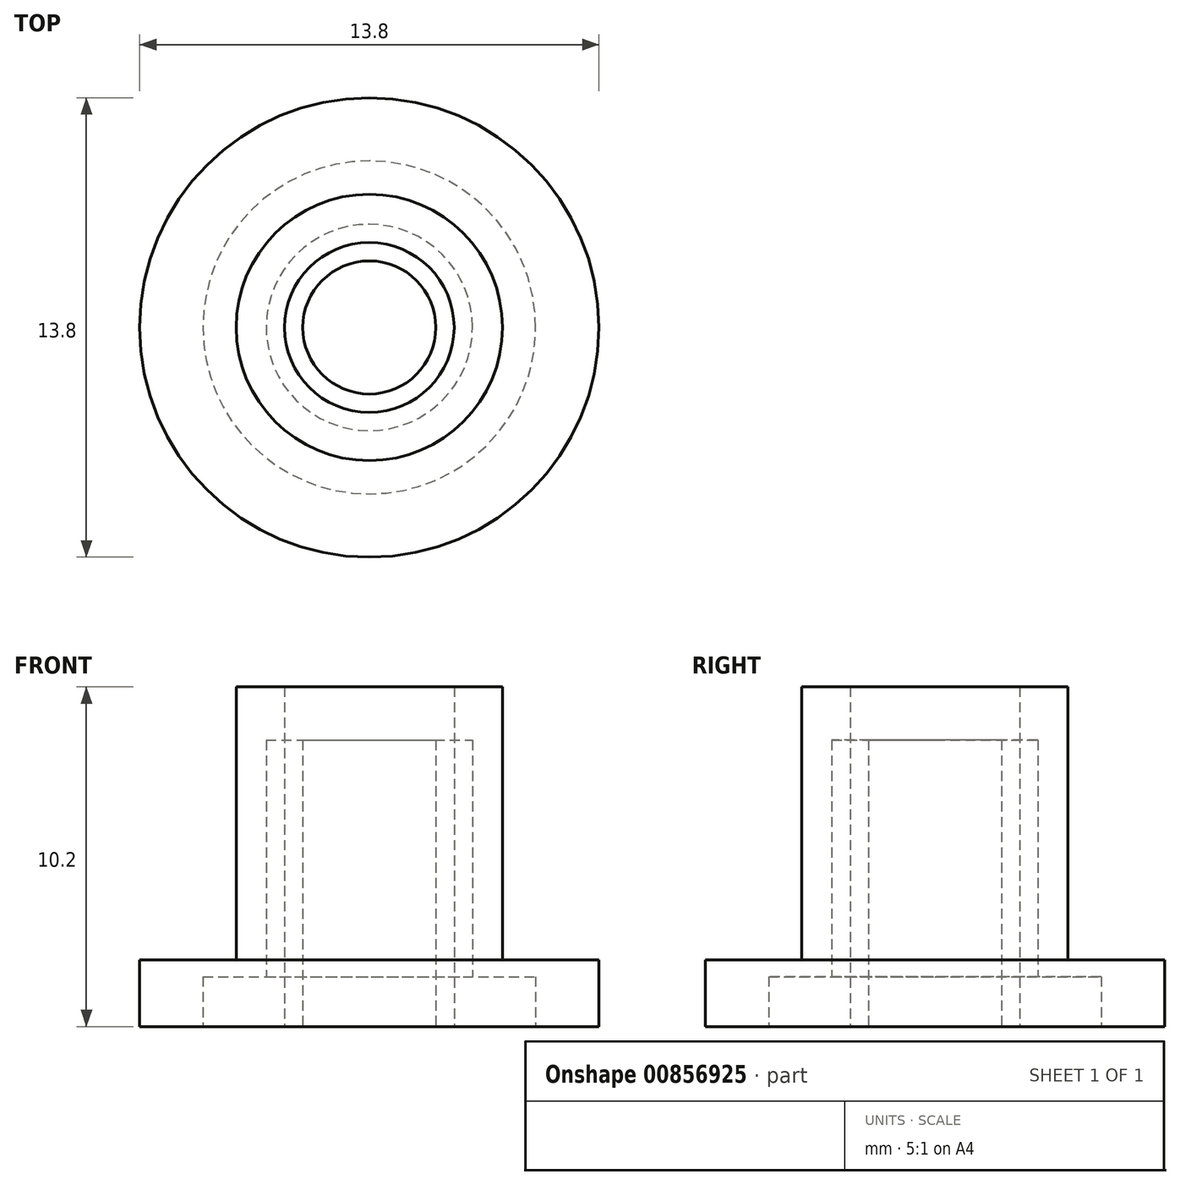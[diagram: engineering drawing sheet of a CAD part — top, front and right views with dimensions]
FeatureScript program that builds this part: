
annotation { "Feature Type Name" : "Feature", "Feature Type Description" : "" }
export const myFeature = defineFeature(function(context is Context, id is Id, definition is map)
    precondition{}
    {
        {
            var Q0;
            Q0=qCreatedBy(makeId("Front.planeOp"),FACE);
            var sketch = newSketch(context, id + "F0", { "sketchPlane" : qUnion([Q0])});
            skLineSegment(sketch, "E0", {"start": v(0, 0) * mm, "end": v(0, 12.5) * mm, "construction": true});
            skLineSegment(sketch, "E1", {"start": v(-2, 0) * mm, "end": v(-2, 8.6) * mm});
            skLineSegment(sketch, "E2", {"start": v(-2, 8.6) * mm, "end": v(-3.1, 8.6) * mm});
            skLineSegment(sketch, "E3", {"start": v(-3.1, 8.6) * mm, "end": v(-3.1, 1.5) * mm});
            skLineSegment(sketch, "E4", {"start": v(-3.1, 1.5) * mm, "end": v(-5, 1.5) * mm});
            skLineSegment(sketch, "E5", {"start": v(-5, 1.5) * mm, "end": v(-5, 0) * mm});
            skLineSegment(sketch, "E6", {"start": v(-5, 0) * mm, "end": v(-2, 0) * mm});
            skSolve(sketch);
        }
        {
            var Q0;
            Q0=makeQuery(id+"F0.imprint","IMPRINT",FACE,{"disambiguationData":[TD([[makeQuery(id+"F0.imprint","IMPRINT",EDGE,{"derivedFrom":sQuery(id+"F0.wireOp",EDGE,"E1")}),1.0]])]});
            var Q1;
            Q1=sQuery(id+"F0.wireOp",EDGE,"E0");
            revolve(context, id + "F1", {"surfaceOperationType" : NewSurfaceOperationType.NEW, "entities" : qUnion([Q0]), "axis" : qUnion([Q1]), "revolveType" : RevolveType.FULL});
        }
        {
            var Q0;
            Q0=qCreatedBy(makeId("Front.planeOp"),FACE);
            var sketch = newSketch(context, id + "F2", { "sketchPlane" : qUnion([Q0])});
            skLineSegment(sketch, "E7", {"start": v(0, 0) * mm, "end": v(0, 9.24) * mm, "construction": true});
            skLineSegment(sketch, "E8", {"start": v(-2.55, 0) * mm, "end": v(-2.55, 10.2) * mm});
            skLineSegment(sketch, "E9", {"start": v(-2.55, 10.2) * mm, "end": v(-4, 10.2) * mm});
            skLineSegment(sketch, "E10", {"start": v(-4, 10.2) * mm, "end": v(-4, 2) * mm});
            skLineSegment(sketch, "E11", {"start": v(-4, 2) * mm, "end": v(-6.9, 2) * mm});
            skLineSegment(sketch, "E12", {"start": v(-6.9, 2) * mm, "end": v(-6.9, 0) * mm});
            skLineSegment(sketch, "E13", {"start": v(-6.9, 0) * mm, "end": v(-2.55, 0) * mm});
            skSolve(sketch);
        }
        {
            var Q0;
            Q0 = qSketchRegion(id + "F2", true);
            var Q1;
            Q1=sQuery(id+"F2.wireOp",EDGE,"E7");
            revolve(context, id + "F3", {"surfaceOperationType" : NewSurfaceOperationType.NEW, "entities" : qUnion([Q0]), "axis" : qUnion([Q1]), "revolveType" : RevolveType.FULL});
        }
    });
